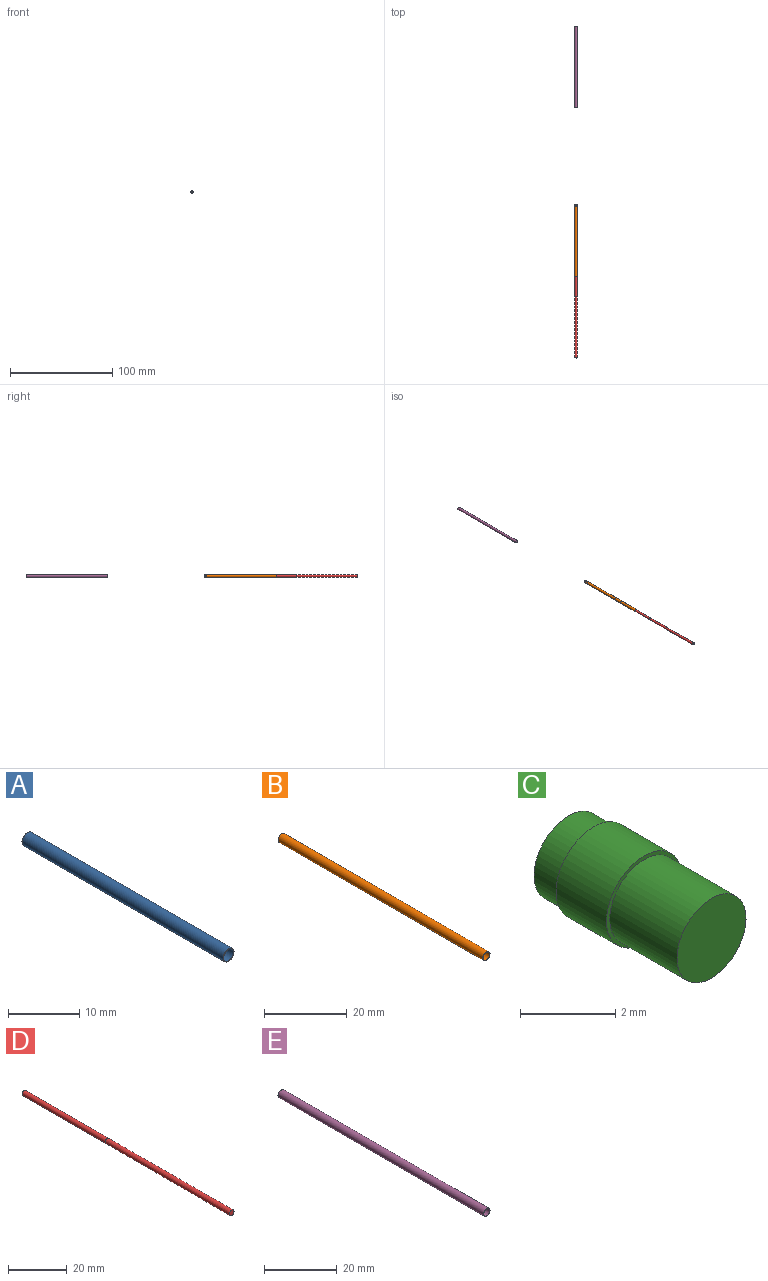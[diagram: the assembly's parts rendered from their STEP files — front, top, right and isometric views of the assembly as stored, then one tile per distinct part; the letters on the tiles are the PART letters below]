
ASSEMBLY  parts=5 mates=4
PART A: 4 faces, bbox 2.2x40x2.2 mm
  f0: cylinder r=0.99mm len=40mm, axis (0,1,0), area 248.8mm2, adj f2,f3
  f1: cylinder r=1.07mm len=40mm, axis (0,1,0), area 270.2mm2, adj f2,f3
  f2: plane 2.15x2.15mm, normal (0,-1,0), area 0.6mm2, adj f0,f1
  f3: plane 2.15x2.15mm, normal (0,1,0), area 0.6mm2, adj f0,f1
PART B: 4 faces, bbox 2.4x70x2.4 mm
  f0: cylinder r=1.12mm len=70mm, axis (0,1,0), area 494.8mm2, adj f2,f3
  f1: cylinder r=1.22mm len=70mm, axis (0,1,0), area 536.6mm2, adj f2,f3
  f2: plane 2.44x2.44mm, normal (0,-1,0), area 0.7mm2, adj f0,f1
  f3: plane 2.44x2.44mm, normal (0,1,0), area 0.7mm2, adj f0,f1
PART C: 7 faces, bbox 2.2x4.3x2.2 mm
  f0: plane 2.05x2.05mm, normal (0,-1,0), area 3.3mm2, adj f6
  f1: plane 2.05x2.05mm, normal (0,1,0), area 3.3mm2, adj f2
  f2: cylinder r=1.03mm len=2.05mm, axis (0,1,0), area 4.8mm2, adj f1,f3
  f3: plane 2.24x2.24mm, normal (0,1,0), area 0.6mm2, adj f2,f4
  f4: cylinder r=1.12mm len=2.24mm, axis (0,1,0), area 10.6mm2, adj f3,f5
  f5: plane 2.24x2.24mm, normal (0,-1,0), area 0.6mm2, adj f4,f6
  f6: cylinder r=1.03mm len=2.05mm, axis (0,1,0), area 12.9mm2, adj f0,f5
PART D: 4 faces, bbox 2.2x100x2.2 mm
  f0: plane 2.2x2.2mm, normal (0,-1,0), area 3.8mm2, adj f3
  f1: plane 1.98x1.98mm, normal (0,1,0), area 3.1mm2, adj f2
  f2: cylinder r=0.99mm len=40mm, axis (0,-1,0), area 248.8mm2, adj f1,f3
  f3: cone r=1.1mm half-angle=0.1deg, axis (0,-1,0), area 394mm2, adj f0,f2
PART E: 4 faces, bbox 2.5x80x2.5 mm
  f0: cylinder r=1.22mm len=80mm, axis (0,1,0), area 615.8mm2, adj f2,f3
  f1: cylinder r=1.26mm len=80mm, axis (0,1,0), area 630.8mm2, adj f2,f3
  f2: plane 2.51x2.51mm, normal (0,-1,0), area 0.2mm2, adj f0,f1
  f3: plane 2.51x2.51mm, normal (0,1,0), area 0.2mm2, adj f0,f1
PLACE A t=(-4.05,24.1,3.89)mm
PLACE B t=(-4.05,26.03,3.89)mm
PLACE C t=(-4.05,26.78,3.89)mm
PLACE D t=(-4.05,-66.13,3.89)mm
PLACE E t=(-4.05,201.25,3.89)mm
MATE slider C.f2 <-> A.f0  axis (0,-1,0) through (-4.05,24.11,3.89)mm
MATE slider D.f2 <-> E.f1  axis (0,-1,0) through (-4.05,-24.08,3.89)mm
MATE slider E.f0 <-> A.f1  axis (0,1,0) through (-4.05,201.25,3.89)mm
MATE slider B.f0 <-> A.f0  axis (0,1,0) through (-4.05,26.03,3.89)mm
